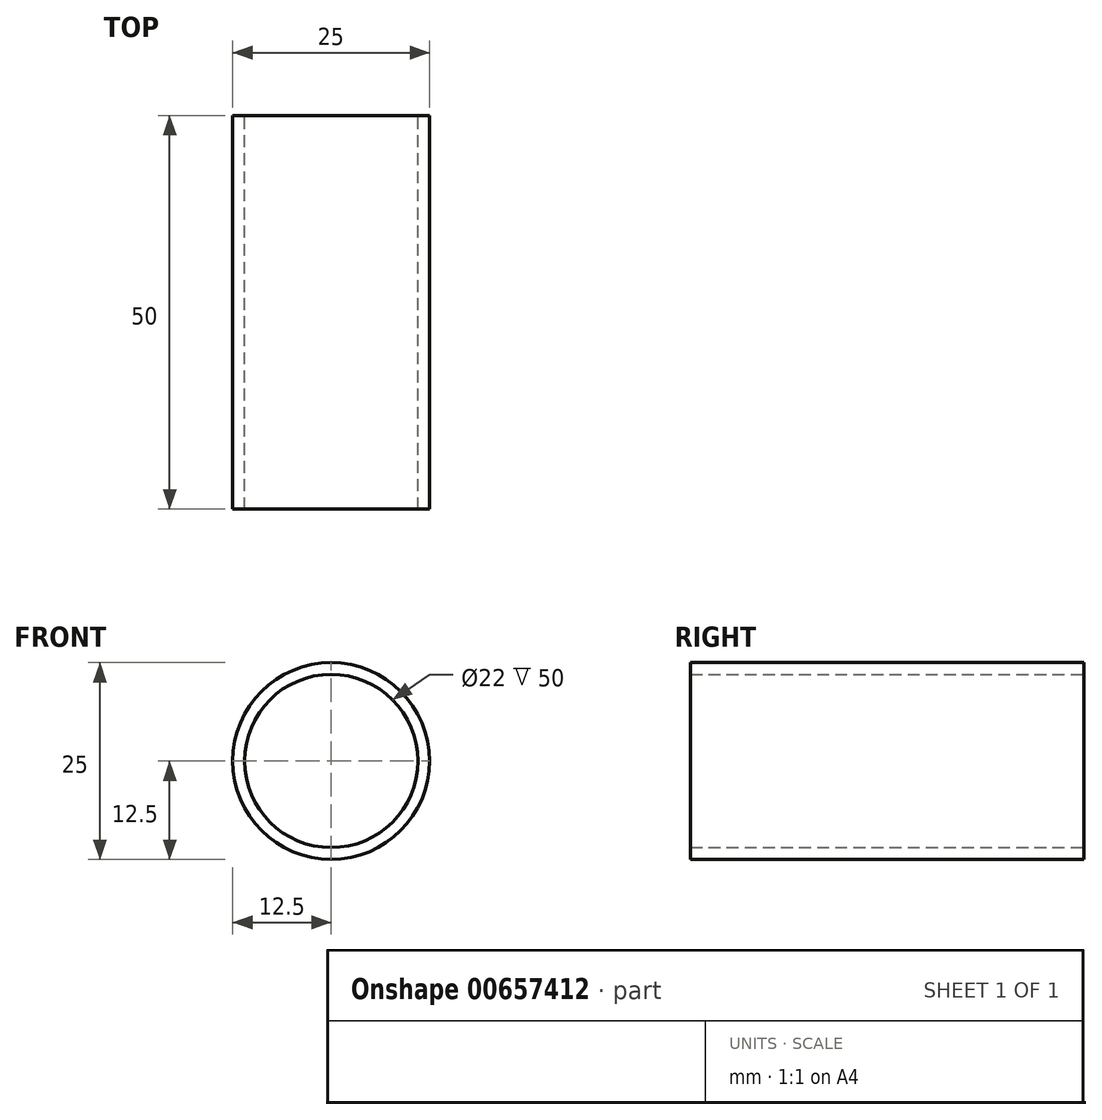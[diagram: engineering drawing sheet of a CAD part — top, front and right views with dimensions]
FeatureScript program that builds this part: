
annotation { "Feature Type Name" : "Feature", "Feature Type Description" : "" }
export const myFeature = defineFeature(function(context is Context, id is Id, definition is map)
    precondition{}
    {
        {
            var Q0;
            Q0=qCreatedBy(makeId("Front.planeOp"),FACE);
            var sketch = newSketch(context, id + "F0", { "sketchPlane" : qUnion([Q0])});
            skCircle(sketch, "E0", {"center": v(0, 0) * mm, "radius": 12.5 * mm});
            skSolve(sketch);
        }
        {
            var Q0;
            Q0=makeQuery(id+"F0.imprint","IMPRINT",FACE,{"disambiguationData":[TD([[makeQuery(id+"F0.imprint","IMPRINT",EDGE,{"derivedFrom":sQuery(id+"F0.wireOp",EDGE,"E0")}),1.0]])]});
            extrude(context, id + "F1", {"entities" : qUnion([Q0]), "depth" : 50 * mm, "offsetDistance" : 25.4 * mm});
        }
        {
            var Q0;
            Q0=qCreatedBy(makeId("Front.planeOp"),FACE);
            var sketch = newSketch(context, id + "F2", { "sketchPlane" : qUnion([Q0])});
            skCircle(sketch, "E1", {"center": v(0, 0) * mm, "radius": 11 * mm});
            skSolve(sketch);
        }
        {
            var Q0;
            Q0=makeQuery(id+"F2.imprint","IMPRINT",FACE,{"disambiguationData":[TD([[makeQuery(id+"F2.imprint","IMPRINT",EDGE,{"derivedFrom":sQuery(id+"F2.wireOp",EDGE,"E1")}),1.0]])]});
            extrude(context, id + "F3", {"entities" : qUnion([Q0]), "operationType" : NewBodyOperationType.REMOVE, "depth" : 50 * mm, "offsetDistance" : 25.4 * mm});
        }
    });
